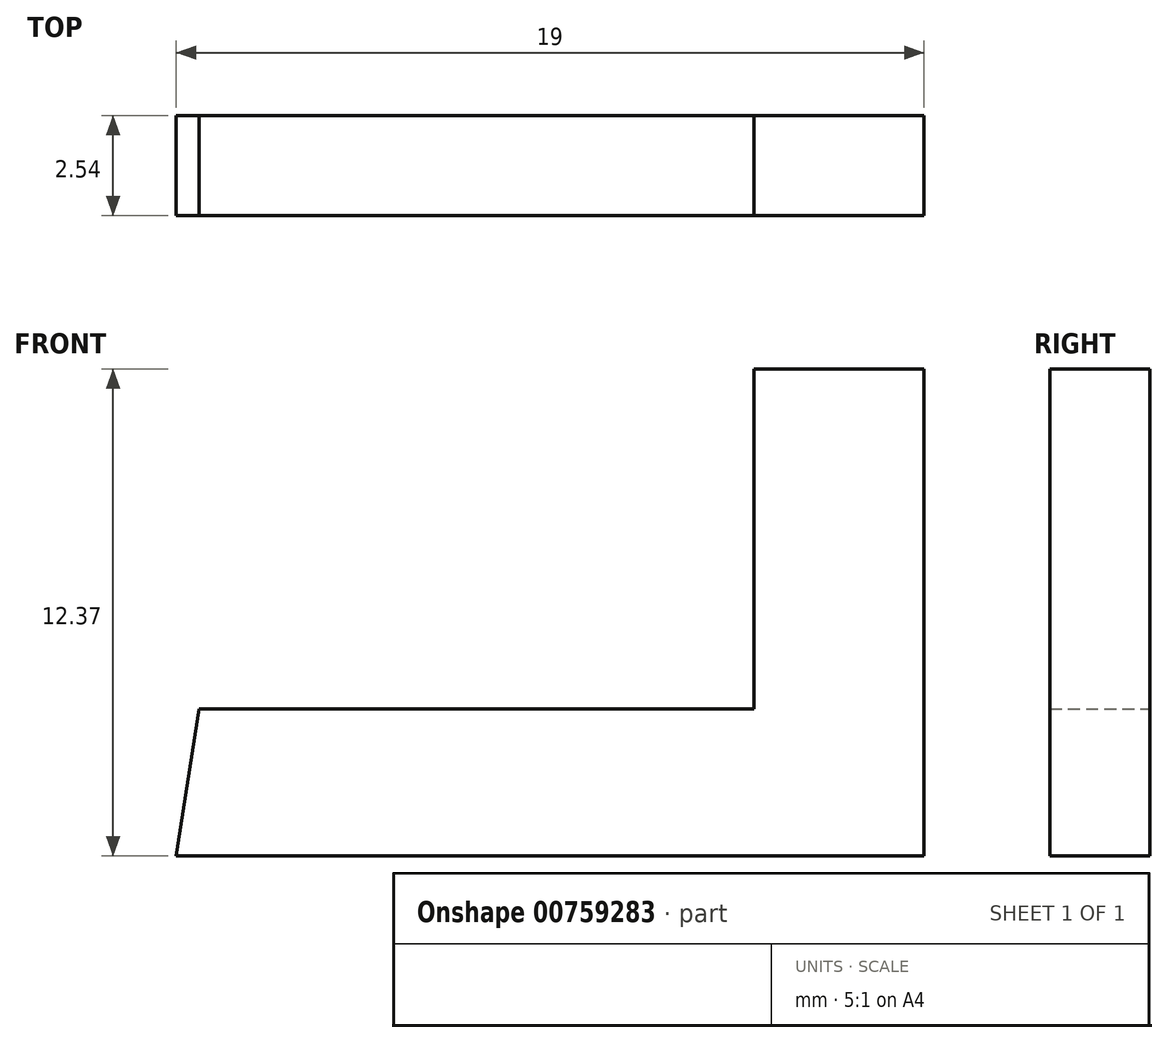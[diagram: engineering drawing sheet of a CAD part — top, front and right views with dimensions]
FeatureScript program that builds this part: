
annotation { "Feature Type Name" : "Feature", "Feature Type Description" : "" }
export const myFeature = defineFeature(function(context is Context, id is Id, definition is map)
    precondition{}
    {
        {
            var Q0;
            Q0=qCreatedBy(makeId("Front.planeOp"),FACE);
            var sketch = newSketch(context, id + "F0", { "sketchPlane" : qUnion([Q0])});
            skLineSegment(sketch, "E0", {"start": v(-39, 23.46) * mm, "end": v(-20, 23.46) * mm});
            skLineSegment(sketch, "E1", {"start": v(-20, 35.83) * mm, "end": v(-20, 23.46) * mm});
            skLineSegment(sketch, "E2", {"start": v(-20, 35.83) * mm, "end": v(-24.32, 35.83) * mm});
            skLineSegment(sketch, "E3", {"start": v(-24.32, 35.83) * mm, "end": v(-24.32, 31.23) * mm});
            skLineSegment(sketch, "E4", {"start": v(-24.32, 31.23) * mm, "end": v(-24.32, 27.2) * mm});
            skLineSegment(sketch, "E5", {"start": v(-38.42, 27.2) * mm, "end": v(-24.32, 27.2) * mm});
            skLineSegment(sketch, "E6", {"start": v(-39, 23.46) * mm, "end": v(-38.42, 27.2) * mm});
            skSolve(sketch);
        }
        {
            var Q0;
            Q0 = qSketchRegion(id + "F0", true);
            extrude(context, id + "F1", {"entities" : qUnion([Q0]), "depth" : 2.54 * mm, "offsetDistance" : 25.4 * mm});
        }
        {
            var Q0;
            Q0=qCreatedBy(makeId("Right.planeOp"),FACE);
            var sketch = newSketch(context, id + "F2", { "sketchPlane" : qUnion([Q0])});
            skCircle(sketch, "E7", {"center": v(0, 48.13) * mm, "radius": 2.67 * mm});
            skSolve(sketch);
        }
        {
            var Q0;
            Q0 = qSketchRegion(id + "F2", true);
            extrude(context, id + "F3", {"entities" : qUnion([Q0]), "operationType" : NewBodyOperationType.REMOVE, "oppositeDirection" : true, "depth" : 2.54 * mm, "offsetDistance" : 25.4 * mm});
        }
        {
            var Q0;
            Q0=qCreatedBy(makeId("Right.planeOp"),FACE);
            var sketch = newSketch(context, id + "F4", { "sketchPlane" : qUnion([Q0])});
            skCircle(sketch, "E8", {"center": v(6.32, 22.36) * mm, "radius": 2.61 * mm});
            skCircle(sketch, "E9", {"center": v(6.32, 22.36) * mm, "radius": 3.3 * mm});
            skSolve(sketch);
        }
        {
            var Q0;
            Q0=sQuery(id+"F4.wireOp",EDGE,"E9");
            extrude(context, id + "F5", {"bodyType" : ToolBodyType.SURFACE, "surfaceEntities" : qUnion([Q0]), "depth" : 5.08 * mm, "offsetDistance" : 25.4 * mm});
        }
    });
